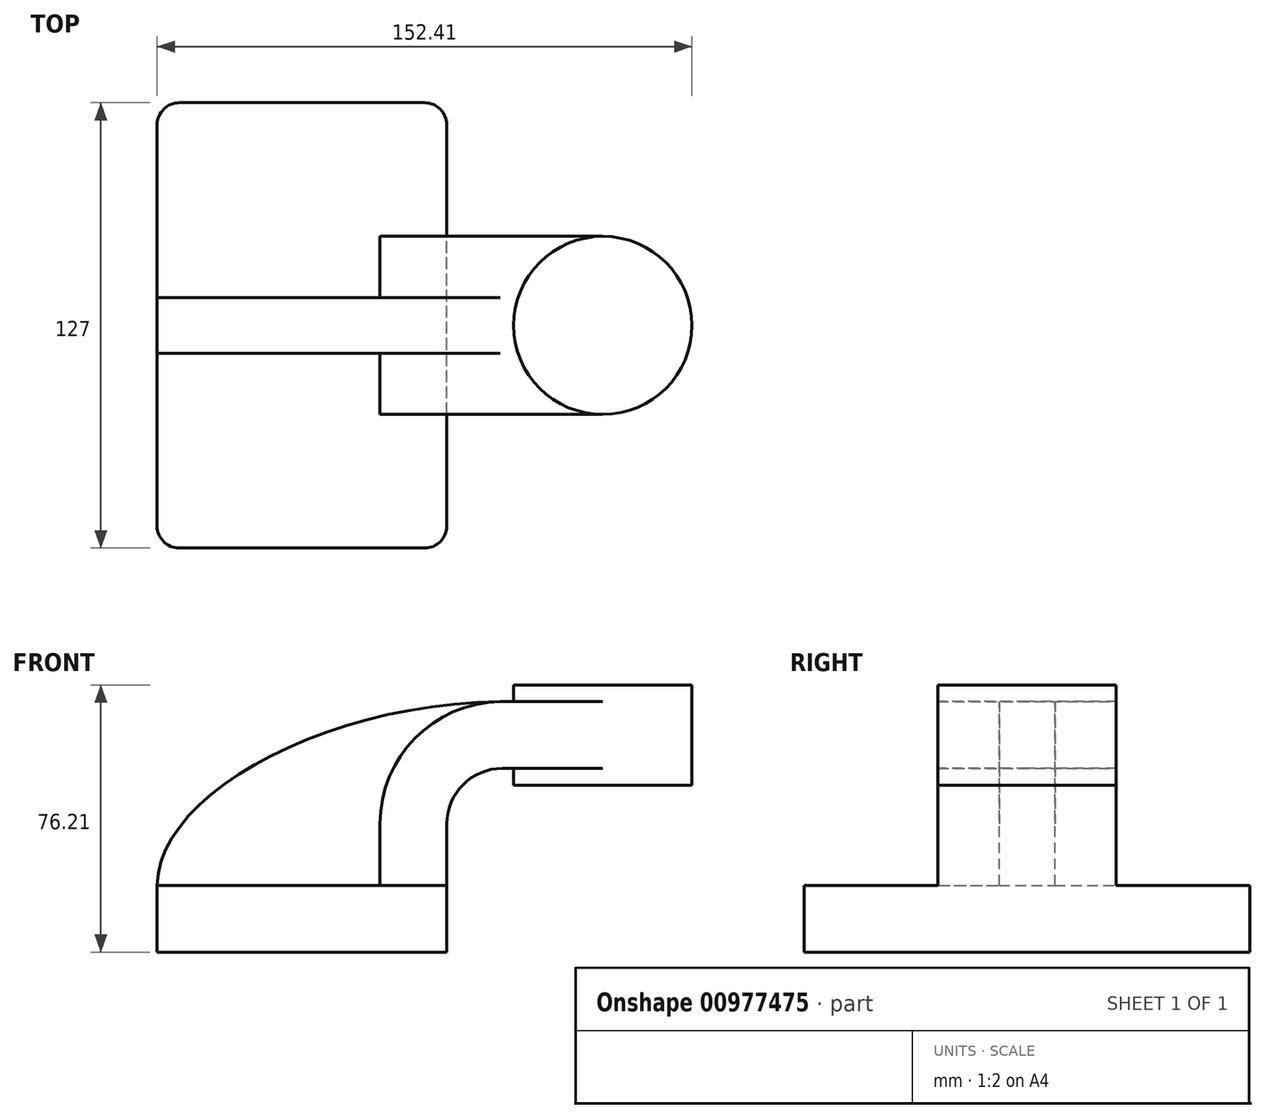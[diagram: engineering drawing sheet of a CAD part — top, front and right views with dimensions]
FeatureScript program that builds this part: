
annotation { "Feature Type Name" : "Feature", "Feature Type Description" : "" }
export const myFeature = defineFeature(function(context is Context, id is Id, definition is map)
    precondition{}
    {
        {
            var Q0;
            Q0=qCreatedBy(makeId("Front.planeOp"),FACE);
            var sketch = newSketch(context, id + "F0", { "sketchPlane" : qUnion([Q0])});
            skLineSegment(sketch, "E0.bottom", {"start": v(-41.28, -9.53) * mm, "end": v(41.28, -9.53) * mm});
            skLineSegment(sketch, "E0.top", {"start": v(-41.28, 9.53) * mm, "end": v(41.28, 9.53) * mm});
            skLineSegment(sketch, "E0.left", {"start": v(-41.28, -9.53) * mm, "end": v(-41.28, 9.53) * mm});
            skLineSegment(sketch, "E0.right", {"start": v(41.28, -9.53) * mm, "end": v(41.28, 9.53) * mm});
            skPoint(sketch, "E0.middle", {"position": v(0, 0) * mm});
            skLineSegment(sketch, "E1.bottom", {"start": v(60.32, 38.1) * mm, "end": v(111.12, 38.1) * mm});
            skLineSegment(sketch, "E1.top", {"start": v(60.32, 66.67) * mm, "end": v(111.12, 66.67) * mm});
            skLineSegment(sketch, "E1.left", {"start": v(60.32, 38.1) * mm, "end": v(60.32, 66.67) * mm});
            skLineSegment(sketch, "E1.right", {"start": v(111.12, 38.1) * mm, "end": v(111.12, 66.67) * mm});
            skPoint(sketch, "E1.middle", {"position": v(85.72, 52.39) * mm});
            skLineSegment(sketch, "E2", {"start": v(41.27, 9.52) * mm, "end": v(41.27, 27) * mm});
            skArc(sketch, "E3", {"start": v(41.27, 27) * mm, "mid": v(45.92, 38.23) * mm, "end": v(57.15, 42.88) * mm});
            skLineSegment(sketch, "E4", {"start": v(57.15, 42.88) * mm, "end": v(85.72, 42.88) * mm});
            skLineSegment(sketch, "E5.0", {"start": v(57.15, 61.93) * mm, "end": v(85.72, 61.93) * mm});
            skArc(sketch, "E5.1", {"start": v(22.22, 27) * mm, "mid": v(32.45, 51.7) * mm, "end": v(57.15, 61.93) * mm});
            skLineSegment(sketch, "E5.2", {"start": v(22.22, 9.52) * mm, "end": v(22.22, 27) * mm});
            skLineSegment(sketch, "E6", {"start": v(85.72, 38.1) * mm, "end": v(85.72, 66.67) * mm});
            skFitSpline(sketch, "E7", {"points": [v(-41.28, 9.52) * mm, v(57.15, 61.93) * mm], "startDerivative": vector(1.12, 78.19) * mm, "endDerivative": vector(151.8, 1.17) * mm});
            skSolve(sketch);
        }
        {
            var Q0;
            Q0=makeQuery(id+"F0.imprint","IMPRINT",FACE,{"disambiguationData":[TD([[makeQuery(id+"F0.imprint","IMPRINT",EDGE,{"derivedFrom":sQuery(id+"F0.wireOp",EDGE,"E0.bottom")}),1.0]])]});
            var Q1;
            Q1=sQuery(id+"F0.wireOp",EDGE,"E0.left");
            var Q2;
            Q2=sQuery(id+"F0.wireOp",EDGE,"E0.bottom");
            var Q3;
            Q3=sQuery(id+"F0.wireOp",EDGE,"E0.top");
            extrude(context, id + "F1", {"entities" : qUnion([Q0]), "surfaceOperationType" : NewSurfaceOperationType.ADD, "surfaceEntities" : qUnion([Q1, Q2, Q3]), "endBound" : BoundingType.SYMMETRIC, "depth" : 127 * mm, "offsetDistance" : 25.4 * mm});
        }
        {
            var Q0;
            {var subQ0=sQuery(id+"F0.wireOp",EDGE,"E4");var subQ1=sQuery(id+"F0.wireOp",EDGE,"E1.left");var subQ2=makeQuery(id+"F0.imprint","INTERSECT",VERTEX,{"derivedFrom":[subQ1,subQ0]});Q0=makeQuery(id+"F0.imprint","IMPRINT",FACE,{"disambiguationData":[TD([[makeQuery(id+"F0.imprint","IMPRINT",EDGE,{"disambiguationData":[TD([[subQ2,-1.0]])],"derivedFrom":subQ1}),-1.0]])]});}
            var Q1;
            {var subQ1=sQuery(id+"F0.wireOp",EDGE,"E2");Q1=makeQuery(id+"F0.imprint","IMPRINT",FACE,{"disambiguationData":[TD([[makeQuery(id+"F0.imprint","IMPRINT",EDGE,{"derivedFrom":subQ1}),1.0]])]});}
            extrude(context, id + "F2", {"entities" : qUnion([Q0, Q1]), "operationType" : NewBodyOperationType.ADD, "endBound" : BoundingType.SYMMETRIC, "depth" : 50.8 * mm, "offsetDistance" : 25.4 * mm});
        }
        {
            var Q0;
            {var subQ3=sQuery(id+"F0.wireOp",EDGE,"E5.2");Q0=makeQuery(id+"F0.imprint","IMPRINT",FACE,{"disambiguationData":[TD([[makeQuery(id+"F0.imprint","IMPRINT",EDGE,{"derivedFrom":subQ3}),1.0]])]});}
            extrude(context, id + "F3", {"entities" : qUnion([Q0]), "operationType" : NewBodyOperationType.ADD, "endBound" : BoundingType.SYMMETRIC, "depth" : 15.88 * mm, "offsetDistance" : 25.4 * mm});
        }
        {
            var Q0;
            {var subQ4=sQuery(id+"F0.wireOp",EDGE,"E1.right");Q0=makeQuery(id+"F0.imprint","IMPRINT",FACE,{"disambiguationData":[TD([[makeQuery(id+"F0.imprint","IMPRINT",EDGE,{"derivedFrom":subQ4}),1.0]])]});}
            var Q1;
            Q1=sQuery(id+"F0.wireOp",EDGE,"E6");
            revolve(context, id + "F4", {"operationType" : NewBodyOperationType.ADD, "surfaceOperationType" : NewSurfaceOperationType.NEW, "entities" : qUnion([Q0]), "axis" : qUnion([Q1]), "revolveType" : RevolveType.FULL});
        }
        {
            var Q0;
            Q0=makeQuery(id+"F1.opExtrude","CAP_EDGE",EDGE,{"disambiguationData":[OSD([sQuery(id+"F0.wireOp",EDGE,"E0.right")])],"isStart":false});
            var Q1;
            Q1=makeQuery(id+"F1.opExtrude","CAP_EDGE",EDGE,{"disambiguationData":[OSD([sQuery(id+"F0.wireOp",EDGE,"E0.left")])],"isStart":false});
            var Q2;
            Q2=makeQuery(id+"F1.opExtrude","CAP_EDGE",EDGE,{"disambiguationData":[OSD([sQuery(id+"F0.wireOp",EDGE,"E0.right")])],"isStart":true});
            var Q3;
            Q3=makeQuery(id+"F1.opExtrude","CAP_EDGE",EDGE,{"disambiguationData":[OSD([sQuery(id+"F0.wireOp",EDGE,"E0.left")])],"isStart":true});
            fillet(context, id + "F5", {"entities" : qUnion([Q0, Q1, Q2, Q3]), "radius" : 6.35 * mm, "tangentPropagation" : true, "allowEdgeOverflow" : false});
        }
    });
